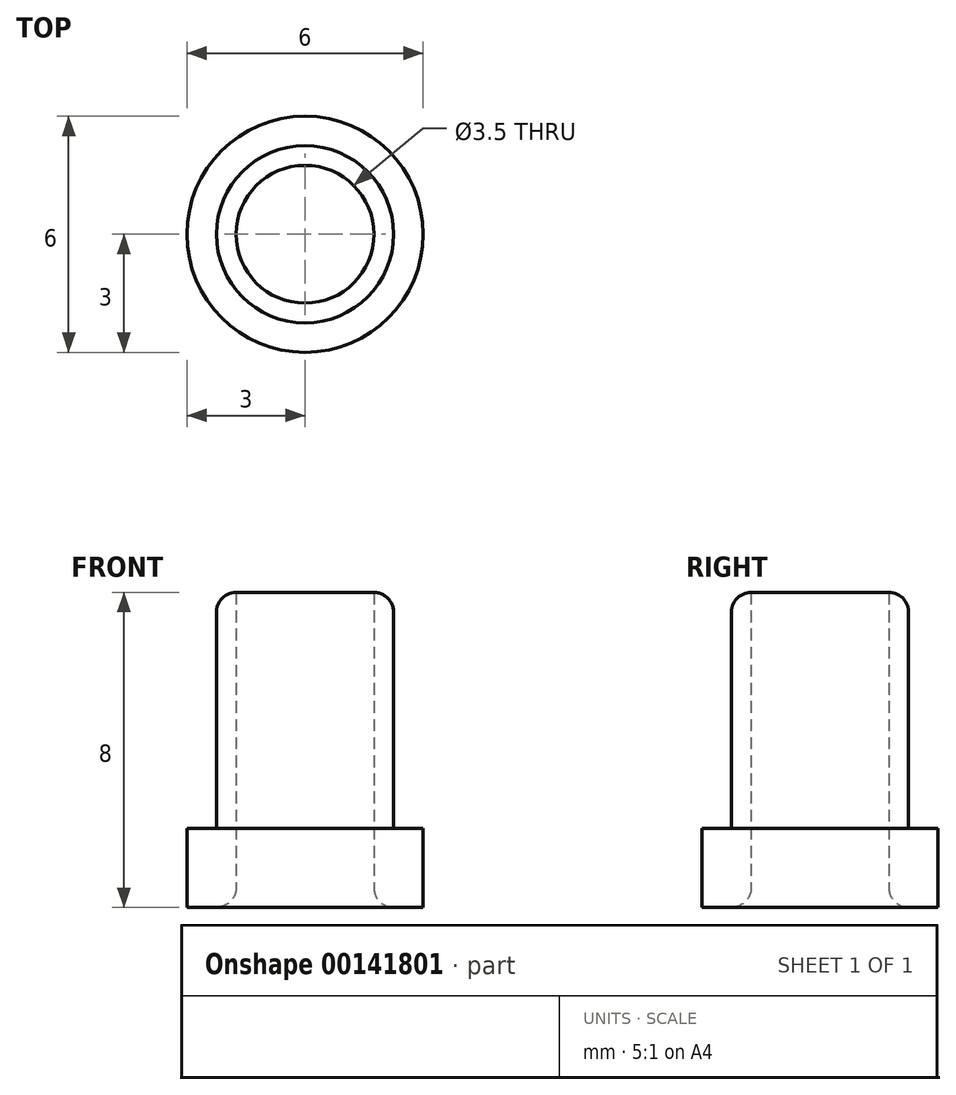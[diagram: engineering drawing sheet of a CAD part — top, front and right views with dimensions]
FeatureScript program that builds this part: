
annotation { "Feature Type Name" : "Feature", "Feature Type Description" : "" }
export const myFeature = defineFeature(function(context is Context, id is Id, definition is map)
    precondition{}
    {
        {
            var Q0;
            Q0=qCreatedBy(makeId("Top.planeOp"),FACE);
            var sketch = newSketch(context, id + "F0", { "sketchPlane" : qUnion([Q0])});
            skCircle(sketch, "E0", {"center": v(0, 0) * mm, "radius": 3 * mm});
            skCircle(sketch, "E1", {"center": v(0, 0) * mm, "radius": 2.25 * mm});
            skCircle(sketch, "E2", {"center": v(0, 0) * mm, "radius": 1.75 * mm});
            skSolve(sketch);
        }
        {
            var Q0;
            Q0=makeQuery(id+"F0.imprint","IMPRINT",FACE,{"disambiguationData":[TD([[makeQuery(id+"F0.imprint","IMPRINT",EDGE,{"derivedFrom":sQuery(id+"F0.wireOp",EDGE,"E0")}),1.0]])]});
            extrude(context, id + "F1", {"entities" : qUnion([Q0]), "depth" : 2 * mm});
        }
        {
            var Q0;
            Q0=makeQuery(id+"F0.imprint","IMPRINT",FACE,{"disambiguationData":[TD([[makeQuery(id+"F0.imprint","IMPRINT",EDGE,{"derivedFrom":sQuery(id+"F0.wireOp",EDGE,"E1")}),1.0]])]});
            extrude(context, id + "F2", {"entities" : qUnion([Q0]), "operationType" : NewBodyOperationType.ADD, "depth" : 8 * mm});
        }
        {
            var Q0;
            Q0=makeQuery(id+"F2.opExtrude","CAP_EDGE",EDGE,{"disambiguationData":[OSD([sQuery(id+"F0.wireOp",EDGE,"E2")])],"isStart":true});
            fillet(context, id + "F3", {"entities" : qUnion([Q0]), "radius" : 0.5 * mm, "allowEdgeOverflow" : false});
        }
        {
            var Q0;
            Q0=makeQuery(id+"F2.opExtrude","CAP_EDGE",EDGE,{"disambiguationData":[OSD([sQuery(id+"F0.wireOp",EDGE,"E1")])],"isStart":false});
            fillet(context, id + "F4", {"entities" : qUnion([Q0]), "radius" : 0.5 * mm, "tangentPropagation" : true, "allowEdgeOverflow" : false});
        }
    });
